# Revit family: PRS
name_source: partatom
category: Lighting Fixtures
units: mm (PartAtom-declared; Revit-internal decimal feet)

## family parameters
Cut with Voids When Loaded = No
Host = Face
Light Source = Yes
OmniClass Number = 23.80.70.14
OmniClass Title = Luminaries for External Lighting
Part Type = Normal
Room Calculation Point = No
Round Connector Dimension = Use Diameter
Shared = Yes

## types (2) — shared parameters
Apparent Load = 60 VA
Assembly Code = D5020200
Certifications = Fixture is IP65 rated,Listed to UL1598 for use in wet locations
Color Filter = 16777215
Connector Description = Lighting Connector
Default Elevation = 48 "
Description = Perimashield PRS
Dimming Lamp Color Temperature Shift = <None>
Features = Non-cutoff retractor fills surrounding area with safety/security illumination
• Durable polycarbonate front housing and lens are impact resistant
• Optional photocontrol for automatic off during daylight hours
• Easy to install by one person
• Environmentally friendly with minimal uplight
Housing Material = Paint - Metallic Bronze Textured
IP Rating = IP65
Lamp = LED
Load Classification = Lighting
Manufacturer = EXO
Power Factor = 1
Reflector Finish = White Glass
Tilt Angle = 180.00°
URL = https://www.currentlighting.com
Voltage = 120 V
Warranty = 5 years Warranty
Wattage Comments = 60W
Watts = 60 W

## per-type parameters (varying)
| type | Photometric Web File |
| PRS-20-4K | PRS-20-4K.ies |
| PRS-20-5K | PRS-20-5K.ies |

note: column(s) folded — value = type name in every type: Model

## geometry (parser evidence)
native form markers: Sweep x5
no freeform markers — native parametric forms only
